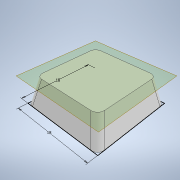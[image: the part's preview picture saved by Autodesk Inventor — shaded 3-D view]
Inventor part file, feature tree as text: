
AUTODESK INVENTOR PART (.ipt)
format: ipt  version: 2022 (Build 260153000, 153)  size: 192,512 bytes
history: native  units: in
note: dims shown in document units (in); Inventor stores cm internally (conversion verified against a paired STEP export)
features: extrude x6, sketch x6, plane x2, fillet x1, split x1
ambient origin geometry x8: Origin, YZ Plane, XZ Plane, XY Plane, X Axis, Y Axis, Z Axis, Center Point
bodies: Solid1 (feature_tree)
feature tree (16):
  extrude  "Extrusion1"  Depth=0.7087in
  fillet  "Fillet1"  Radius=0.315in
  plane  "Work Plane1"
  extrude  "Extrusion2"  Depth=0.7087in
  extrude  "Extrusion3"  Depth=0.6299in
  extrude  "Extrusion4"  Depth=0.1772in
  extrude  "Extrusion5"  Depth=0.1575in TaperAngle=0.0deg
  plane  "Work Plane3"
  split  "Split1"
  extrude  "Extrusion7"  Depth=0.1634in
  sketch  "Sketch1"  dims[d0=0.7087in d1=0.7087in d2=0.315in d3=-0.1031in]
  sketch  "Sketch2"  dims[d4=0.0591in d5=0.7087in]
  sketch  "Sketch3"  dims[d6=0.0in d7=0.0in d8=0.6299in]
  sketch  "Sketch4"  dims[d9=0.6299in d10=0.1772in d11=-0.1031in]
  sketch  "Sketch5"  dims[d12=0.2185in d13=0.1575in d14=0.0in]
  sketch  "Sketch7"  dims[d15=0.0472in d16=0.1634in d17=0.1634in d18=0.0472in d19=0.0118in d20=0.1575in d21=0.0in d24=-0.2362in d25=0.3937in d26=0.0in]
